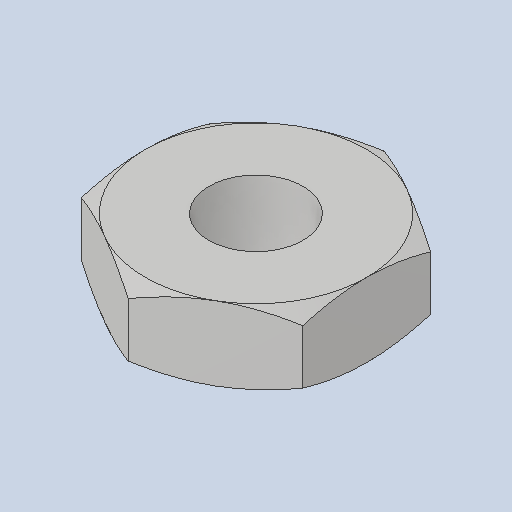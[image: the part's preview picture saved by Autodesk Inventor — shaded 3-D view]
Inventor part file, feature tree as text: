
AUTODESK INVENTOR PART (.ipt)
format: ipt  version: 2023.4 (Build 274418000, 418)  size: 115,712 bytes
history: native  units: in
note: dims shown in document units (in); Inventor stores cm internally (conversion verified against a paired STEP export)
features: mirror x1
ambient origin geometry x8: Origin, YZ Plane, XZ Plane, XY Plane, X Axis, Y Axis, Z Axis, Center Point
bodies: Solid1 (feature_tree)
feature tree (1):
  mirror  "Mirror1"
